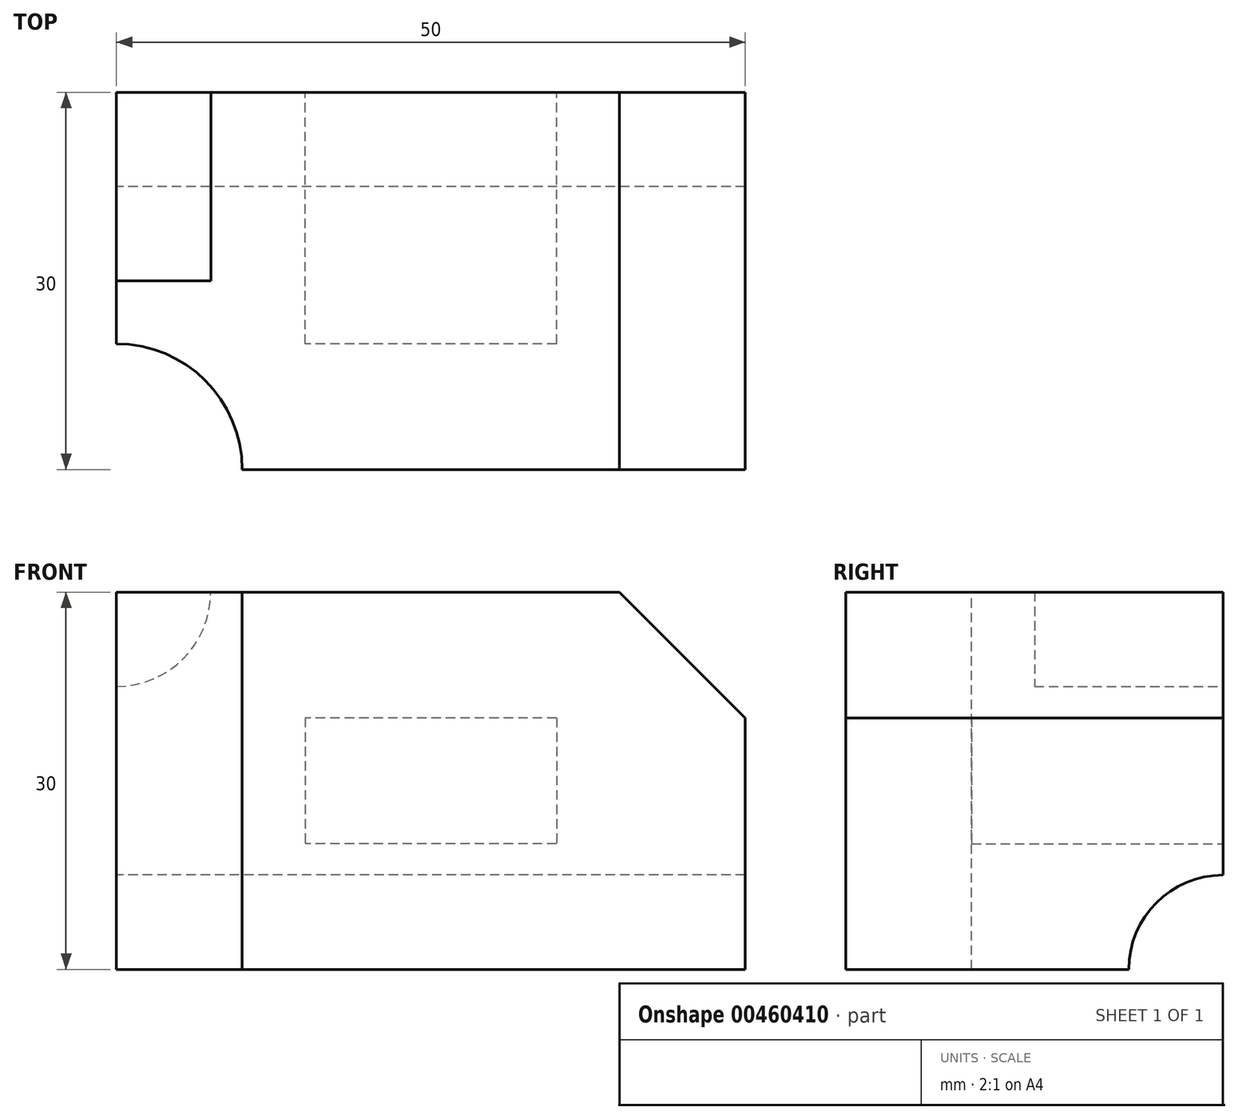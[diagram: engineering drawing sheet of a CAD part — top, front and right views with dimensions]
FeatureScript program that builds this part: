
annotation { "Feature Type Name" : "Feature", "Feature Type Description" : "" }
export const myFeature = defineFeature(function(context is Context, id is Id, definition is map)
    precondition{}
    {
        {
            var Q0;
            Q0=qCreatedBy(makeId("Top.planeOp"),FACE);
            var sketch = newSketch(context, id + "F0", { "sketchPlane" : qUnion([Q0])});
            skLineSegment(sketch, "E0.bottom", {"start": v(-63.13, 55.86) * mm, "end": v(66.17, 55.86) * mm});
            skLineSegment(sketch, "E0.top", {"start": v(-63.13, -54.13) * mm, "end": v(66.17, -54.13) * mm});
            skLineSegment(sketch, "E0.left", {"start": v(-63.13, 55.86) * mm, "end": v(-63.13, -54.13) * mm});
            skLineSegment(sketch, "E0.right", {"start": v(66.17, 55.86) * mm, "end": v(66.17, -54.13) * mm});
            skSolve(sketch);
        }
        {
            var Q0;
            Q0=makeQuery(id+"F0.imprint","IMPRINT",FACE,{"disambiguationData":[TD([[makeQuery(id+"F0.imprint","IMPRINT",EDGE,{"derivedFrom":sQuery(id+"F0.wireOp",EDGE,"E0.bottom")}),-1.0]])]});
            var sketch = newSketch(context, id + "F1", { "sketchPlane" : qUnion([Q0])});
            skLineSegment(sketch, "E1.bottom", {"start": v(-22.72, 12.42) * mm, "end": v(27.28, 12.42) * mm});
            skLineSegment(sketch, "E1.top", {"start": v(-22.72, -17.58) * mm, "end": v(27.28, -17.58) * mm});
            skLineSegment(sketch, "E1.left", {"start": v(-22.72, 12.42) * mm, "end": v(-22.72, -17.58) * mm});
            skLineSegment(sketch, "E1.right", {"start": v(27.28, 12.42) * mm, "end": v(27.28, -17.58) * mm});
            skSolve(sketch);
        }
        {
            var Q0;
            Q0 = qSketchRegion(id + "F1", true);
            extrude(context, id + "F2", {"entities" : qUnion([Q0]), "depth" : 30 * mm});
        }
        {
            var Q0;
            Q0=makeQuery(id+"F2.opExtrude","SWEPT_FACE",FACE,{"disambiguationData":[OSD([sQuery(id+"F1.wireOp",EDGE,"E1.left")])]});
            var sketch = newSketch(context, id + "F3", { "sketchPlane" : qUnion([Q0])});
            skCircle(sketch, "E2", {"center": v(-12.42, 0) * mm, "radius": 7.5 * mm});
            skSolve(sketch);
        }
        {
            var Q0;
            {var subQ0=sQuery(id+"F3.wireOp",EDGE,"E2");var subQ1=sQuery(id+"F1.wireOp",EDGE,"E1.left");var subQ4=makeQuery(id+"F2.opExtrude","CAP_EDGE",EDGE,{"disambiguationData":[OSD([subQ1])],"isStart":true});var subQ5=makeQuery(id+"F3.imprint","INTERSECT",VERTEX,{"derivedFrom":[subQ4,subQ0]});Q0=makeQuery(id+"F3.imprint","IMPRINT",FACE,{"disambiguationData":[TD([[makeQuery(id+"F3.imprint","IMPRINT",EDGE,{"disambiguationData":[TD([[subQ5,1.0]])],"derivedFrom":subQ0}),1.0]])]});}
            var Q1;
            {var subQ0=sQuery(id+"F3.wireOp",EDGE,"E2");var subQ1=sQuery(id+"F1.wireOp",EDGE,"E1.left");var subQ4=makeQuery(id+"F2.opExtrude","CAP_EDGE",EDGE,{"disambiguationData":[OSD([subQ1])],"isStart":true});var subQ5=makeQuery(id+"F3.imprint","INTERSECT",VERTEX,{"derivedFrom":[subQ4,subQ0]});Q1=makeQuery(id+"F3.imprint","IMPRINT",FACE,{"disambiguationData":[TD([[makeQuery(id+"F3.imprint","IMPRINT",EDGE,{"disambiguationData":[TD([[subQ5,-1.0]])],"derivedFrom":subQ0}),1.0]])]});}
            extrude(context, id + "F4", {"entities" : qUnion([Q0, Q1]), "operationType" : NewBodyOperationType.REMOVE, "oppositeDirection" : true, "depth" : 50 * mm});
        }
        {
            var Q0;
            Q0=makeQuery(id+"F2.opExtrude","SWEPT_FACE",FACE,{"disambiguationData":[OSD([sQuery(id+"F1.wireOp",EDGE,"E1.bottom")])]});
            var sketch = newSketch(context, id + "F5", { "sketchPlane" : qUnion([Q0])});
            skLineSegment(sketch, "E3", {"start": v(-27.28, 30) * mm, "end": v(-27.28, 20) * mm});
            skLineSegment(sketch, "E4", {"start": v(-27.28, 20) * mm, "end": v(-17.28, 30) * mm});
            skLineSegment(sketch, "E5", {"start": v(-17.28, 30) * mm, "end": v(-27.28, 30) * mm});
            skSolve(sketch);
        }
        {
            var Q0;
            Q0=makeQuery(id+"F5.imprint","IMPRINT",FACE,{"disambiguationData":[TD([[makeQuery(id+"F5.imprint","IMPRINT",EDGE,{"derivedFrom":sQuery(id+"F5.wireOp",EDGE,"E3")}),1.0]])]});
            extrude(context, id + "F6", {"entities" : qUnion([Q0]), "operationType" : NewBodyOperationType.REMOVE, "oppositeDirection" : true, "depth" : 30 * mm});
        }
        {
            var Q0;
            Q0=makeQuery(id+"F2.opExtrude","SWEPT_FACE",FACE,{"disambiguationData":[OSD([sQuery(id+"F1.wireOp",EDGE,"E1.bottom")])]});
            var sketch = newSketch(context, id + "F7", { "sketchPlane" : qUnion([Q0])});
            skCircle(sketch, "E6", {"center": v(22.72, 30) * mm, "radius": 7.5 * mm});
            skSolve(sketch);
        }
        {
            var Q0;
            {var subQ0=sQuery(id+"F7.wireOp",EDGE,"E6");var subQ1=sQuery(id+"F1.wireOp",EDGE,"E1.bottom");var subQ4=makeQuery(id+"F2.opExtrude","CAP_EDGE",EDGE,{"disambiguationData":[OSD([subQ1])],"isStart":false});var subQ5=makeQuery(id+"F7.imprint","INTERSECT",VERTEX,{"derivedFrom":[subQ4,subQ0]});Q0=makeQuery(id+"F7.imprint","IMPRINT",FACE,{"disambiguationData":[TD([[makeQuery(id+"F7.imprint","IMPRINT",EDGE,{"disambiguationData":[TD([[subQ5,-1.0]])],"derivedFrom":subQ0}),1.0]])]});}
            extrude(context, id + "F8", {"entities" : qUnion([Q0]), "operationType" : NewBodyOperationType.REMOVE, "oppositeDirection" : true, "depth" : 15 * mm});
        }
        {
            var Q0;
            Q0=makeQuery(id+"F2.opExtrude","CAP_FACE",FACE,{"disambiguationData":[OSD([sQuery(id+"F1.wireOp",EDGE,"E1.bottom"),sQuery(id+"F1.wireOp",EDGE,"E1.top"),sQuery(id+"F1.wireOp",EDGE,"E1.left"),sQuery(id+"F1.wireOp",EDGE,"E1.right")])],"isStart":false});
            var sketch = newSketch(context, id + "F9", { "sketchPlane" : qUnion([Q0])});
            skCircle(sketch, "E7", {"center": v(-22.72, -17.58) * mm, "radius": 10 * mm});
            skSolve(sketch);
        }
        {
            var Q0;
            {var subQ0=sQuery(id+"F9.wireOp",EDGE,"E7");var subQ1=makeQuery(id+"F2.opExtrude","CAP_EDGE",EDGE,{"disambiguationData":[OSD([sQuery(id+"F1.wireOp",EDGE,"E1.top")])],"isStart":false});var subQ2=makeQuery(id+"F9.imprint","INTERSECT",VERTEX,{"derivedFrom":[subQ1,subQ0]});Q0=makeQuery(id+"F9.imprint","IMPRINT",FACE,{"disambiguationData":[TD([[makeQuery(id+"F9.imprint","IMPRINT",EDGE,{"disambiguationData":[TD([[subQ2,-1.0]])],"derivedFrom":subQ0}),1.0]])]});}
            extrude(context, id + "F10", {"entities" : qUnion([Q0]), "operationType" : NewBodyOperationType.REMOVE, "oppositeDirection" : true, "depth" : 30 * mm});
        }
        {
            var Q0;
            Q0=makeQuery(id+"F2.opExtrude","SWEPT_FACE",FACE,{"disambiguationData":[OSD([sQuery(id+"F1.wireOp",EDGE,"E1.bottom")])]});
            var sketch = newSketch(context, id + "F11", { "sketchPlane" : qUnion([Q0])});
            skLineSegment(sketch, "E8.bottom", {"start": v(-12.28, 20) * mm, "end": v(7.72, 20) * mm});
            skLineSegment(sketch, "E8.top", {"start": v(-12.28, 10) * mm, "end": v(7.72, 10) * mm});
            skLineSegment(sketch, "E8.left", {"start": v(-12.28, 20) * mm, "end": v(-12.28, 10) * mm});
            skLineSegment(sketch, "E8.right", {"start": v(7.72, 20) * mm, "end": v(7.72, 10) * mm});
            skSolve(sketch);
        }
        {
            var Q0;
            Q0=makeQuery(id+"F11.imprint","IMPRINT",FACE,{"disambiguationData":[TD([[makeQuery(id+"F11.imprint","IMPRINT",EDGE,{"derivedFrom":sQuery(id+"F11.wireOp",EDGE,"E8.bottom")}),-1.0]])]});
            extrude(context, id + "F12", {"entities" : qUnion([Q0]), "operationType" : NewBodyOperationType.REMOVE, "oppositeDirection" : true, "depth" : 20 * mm});
        }
    });
